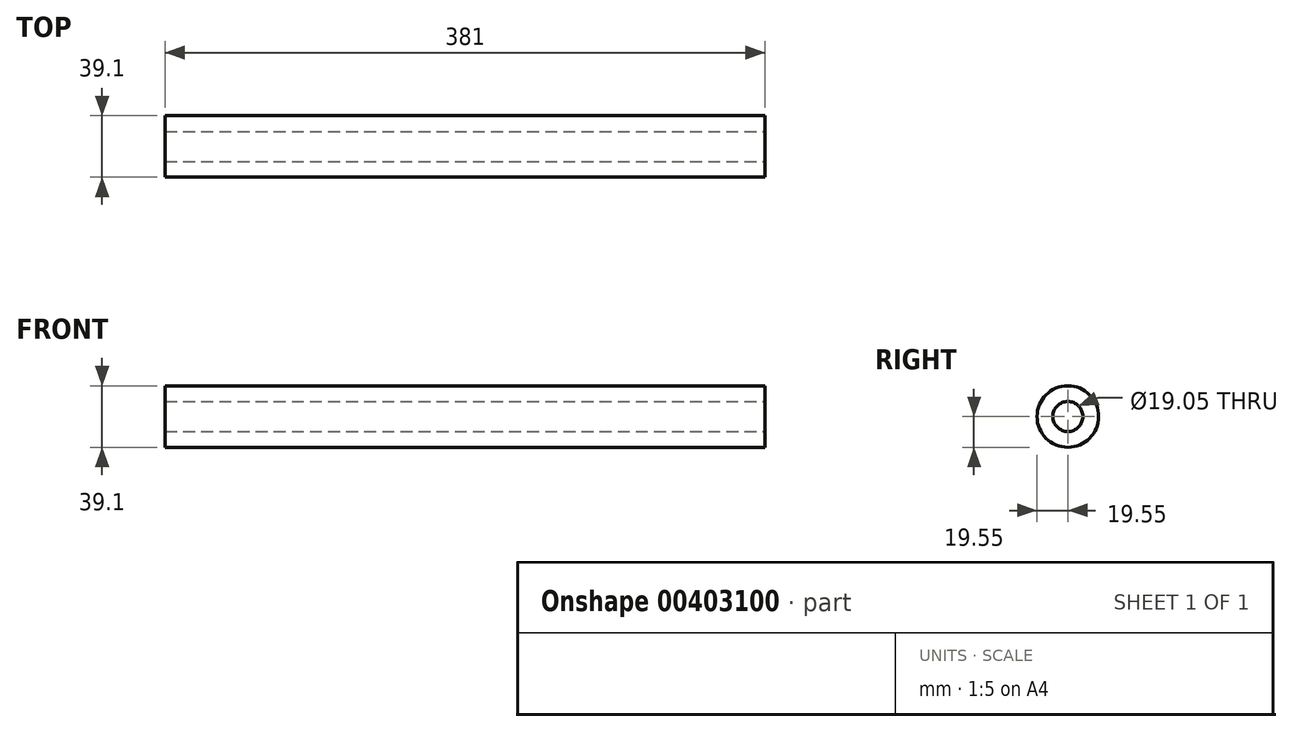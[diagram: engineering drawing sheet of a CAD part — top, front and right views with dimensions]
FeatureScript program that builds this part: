
annotation { "Feature Type Name" : "Feature", "Feature Type Description" : "" }
export const myFeature = defineFeature(function(context is Context, id is Id, definition is map)
    precondition{}
    {
        {
            var Q0;
            Q0=qCreatedBy(makeId("Right.planeOp"),FACE);
            var sketch = newSketch(context, id + "F0", { "sketchPlane" : qUnion([Q0])});
            skCircle(sketch, "E0", {"center": v(0, 0) * mm, "radius": 19.55 * mm});
            skSolve(sketch);
        }
        {
            var Q0;
            Q0=makeQuery(id+"F0.imprint","IMPRINT",FACE,{"disambiguationData":[TD([[makeQuery(id+"F0.imprint","IMPRINT",EDGE,{"derivedFrom":sQuery(id+"F0.wireOp",EDGE,"E0")}),1.0]])]});
            var Q1;
            Q1=sQuery(id+"F0.wireOp",EDGE,"E0");
            extrude(context, id + "F1", {"entities" : qUnion([Q0]), "surfaceEntities" : qUnion([Q1]), "depth" : 127 * mm});
        }
        {
            var Q0;
            Q0=makeQuery(id+"F1.opExtrude","CAP_FACE",FACE,{"disambiguationData":[OSD([sQuery(id+"F0.wireOp",EDGE,"E0")])],"isStart":false});
            var sketch = newSketch(context, id + "F2", { "sketchPlane" : qUnion([Q0])});
            skPoint(sketch, "E1", {"position": v(0, 0) * mm});
            skSolve(sketch);
        }
        {
            var Q0;
            Q0=sQuery(id+"F2.wireOp",VERTEX,"E1");
            var Q1;
            Q1=makeQuery(id+"F1.opExtrude","SWEPT_BODY",BODY,{"disambiguationData":[OSD([sQuery(id+"F0.wireOp",EDGE,"E0")])]});
            hole(context, id + "F3", {"style" : HoleStyle.SIMPLE, "endStyle" : HoleEndStyle.THROUGH, "holeDiameter" : 19.05 * mm, "isTappedThrough" : true, "tappedDepth" : 12.7 * mm, "tapClearance" : 3, "locations" : qUnion([Q0]), "scope" : qUnion([Q1])});
        }
        {
            var Q0;
            Q0=makeQuery(id+"F1.opExtrude","CAP_FACE",FACE,{"disambiguationData":[OSD([sQuery(id+"F0.wireOp",EDGE,"E0")])],"isStart":false});
            extrude(context, id + "F4", {"entities" : qUnion([Q0]), "operationType" : NewBodyOperationType.ADD, "depth" : 254 * mm});
        }
    });
